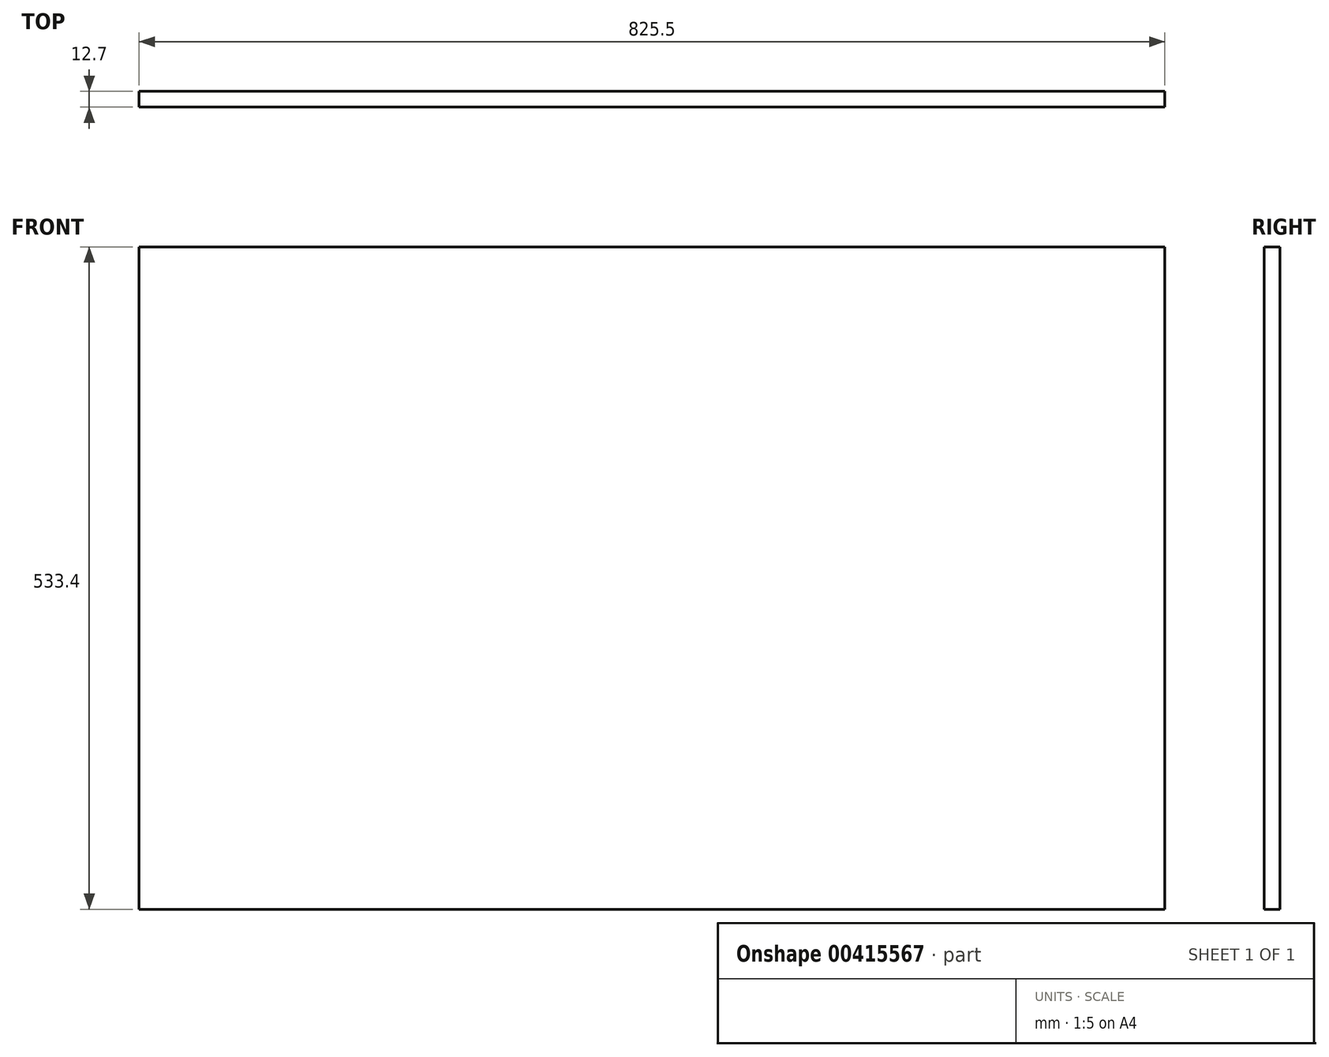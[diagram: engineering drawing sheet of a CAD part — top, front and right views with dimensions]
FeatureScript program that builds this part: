
annotation { "Feature Type Name" : "Feature", "Feature Type Description" : "" }
export const myFeature = defineFeature(function(context is Context, id is Id, definition is map)
    precondition{}
    {
        {
            var Q0;
            Q0=qCreatedBy(makeId("Front.planeOp"),FACE);
            var sketch = newSketch(context, id + "F0", { "sketchPlane" : qUnion([Q0])});
            skLineSegment(sketch, "E0.bottom", {"start": v(412.75, 266.7) * mm, "end": v(-412.75, 266.7) * mm});
            skLineSegment(sketch, "E0.top", {"start": v(412.75, -266.7) * mm, "end": v(-412.75, -266.7) * mm});
            skLineSegment(sketch, "E0.left", {"start": v(412.75, 266.7) * mm, "end": v(412.75, -266.7) * mm});
            skLineSegment(sketch, "E0.right", {"start": v(-412.75, 266.7) * mm, "end": v(-412.75, -266.7) * mm});
            skPoint(sketch, "E0.middle", {"position": v(0, 0) * mm});
            skSolve(sketch);
        }
        {
            var Q0;
            Q0=makeQuery(id+"F0.imprint","IMPRINT",FACE,{"disambiguationData":[TD([[makeQuery(id+"F0.imprint","IMPRINT",EDGE,{"derivedFrom":sQuery(id+"F0.wireOp",EDGE,"E0.bottom")}),1.0]])]});
            extrude(context, id + "F1", {"entities" : qUnion([Q0]), "depth" : 12.7 * mm});
        }
    });
